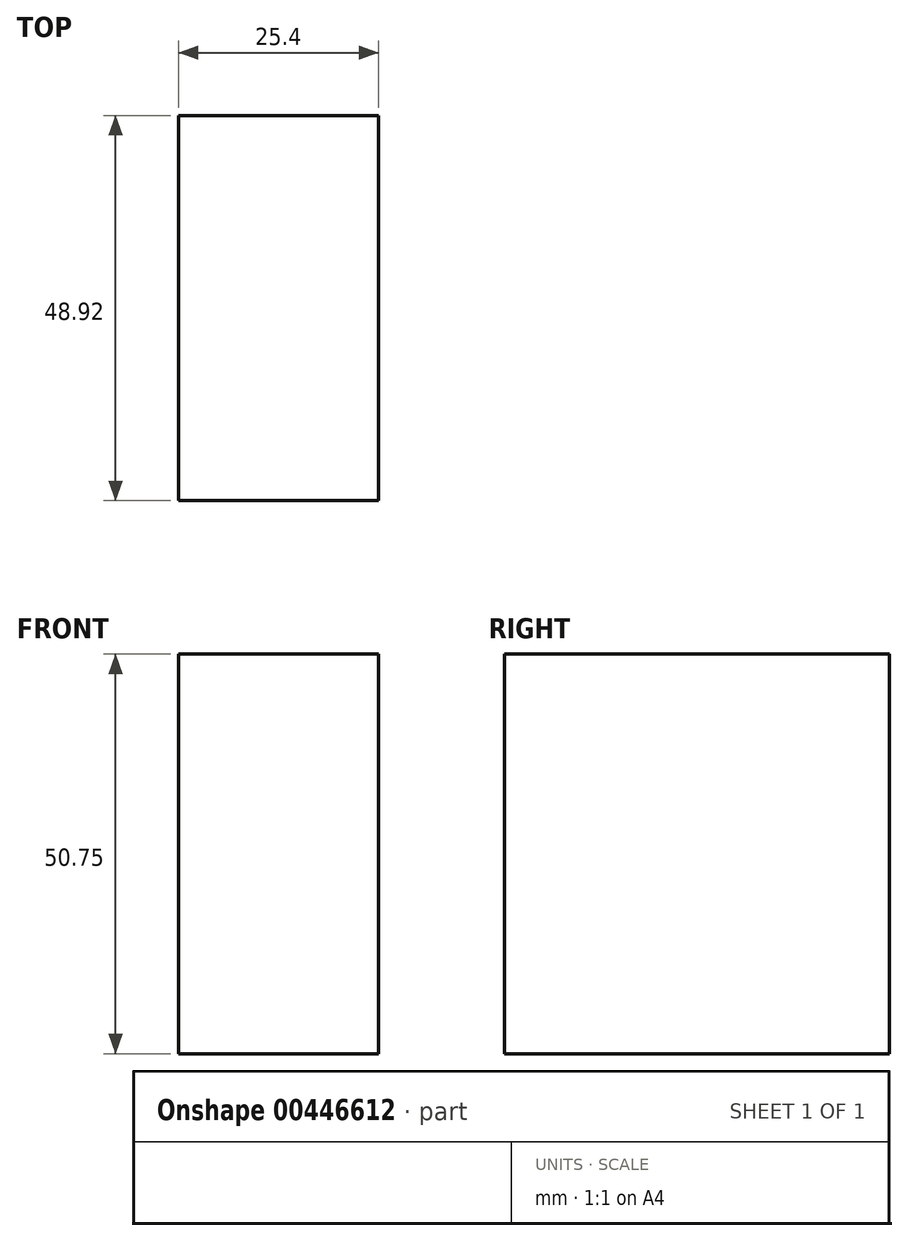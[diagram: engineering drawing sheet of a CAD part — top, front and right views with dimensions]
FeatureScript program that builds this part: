
annotation { "Feature Type Name" : "Feature", "Feature Type Description" : "" }
export const myFeature = defineFeature(function(context is Context, id is Id, definition is map)
    precondition{}
    {
        {
            var Q0;
            Q0=qCreatedBy(makeId("Right.planeOp"),FACE);
            var sketch = newSketch(context, id + "F0", { "sketchPlane" : qUnion([Q0])});
            skLineSegment(sketch, "E0", {"start": v(0, -70.89) * mm, "end": v(0, 61.11) * mm, "construction": true});
            skLineSegment(sketch, "E1.bottom", {"start": v(-64.73, 38.06) * mm, "end": v(-15.81, 38.06) * mm});
            skLineSegment(sketch, "E1.top", {"start": v(-64.73, -12.69) * mm, "end": v(-15.81, -12.69) * mm});
            skLineSegment(sketch, "E1.left", {"start": v(-64.73, 38.06) * mm, "end": v(-64.73, -12.69) * mm});
            skLineSegment(sketch, "E1.right", {"start": v(-15.81, 38.06) * mm, "end": v(-15.81, -12.69) * mm});
            skSolve(sketch);
        }
        {
            var Q0;
            Q0 = qSketchRegion(id + "F0", true);
            extrude(context, id + "F1", {"entities" : qUnion([Q0]), "depth" : 25.4 * mm});
        }
    });
